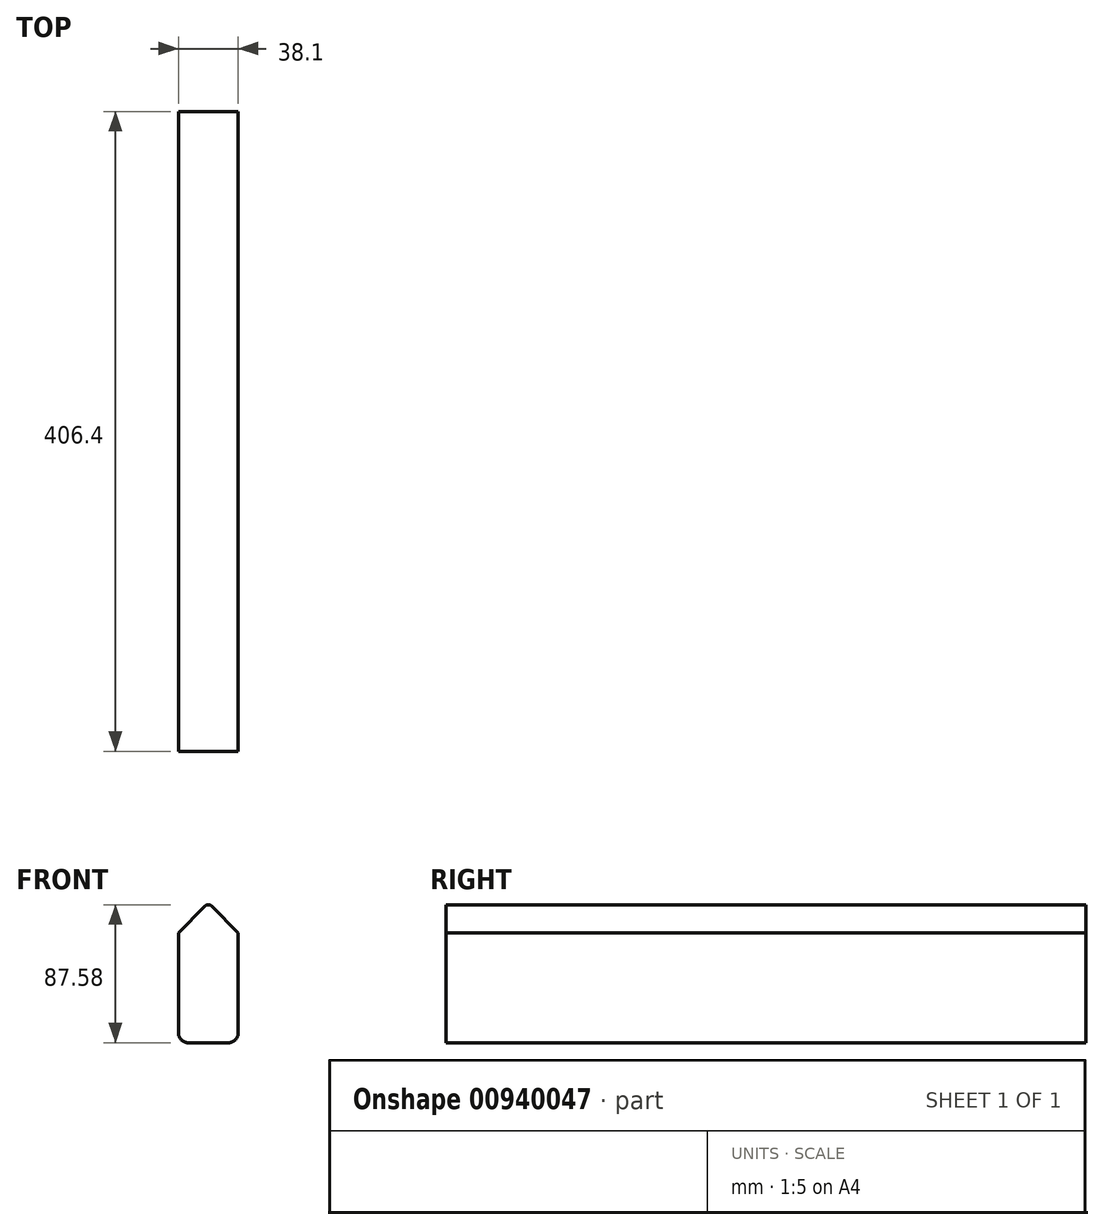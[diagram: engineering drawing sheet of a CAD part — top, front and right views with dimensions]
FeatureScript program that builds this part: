
annotation { "Feature Type Name" : "Feature", "Feature Type Description" : "" }
export const myFeature = defineFeature(function(context is Context, id is Id, definition is map)
    precondition{}
    {
        {
            var Q0;
            Q0=qCreatedBy(makeId("Front.planeOp"),FACE);
            var sketch = newSketch(context, id + "F0", { "sketchPlane" : qUnion([Q0])});
            skLineSegment(sketch, "E0.top", {"start": v(12.7, -44.45) * mm, "end": v(-12.7, -44.45) * mm});
            skLineSegment(sketch, "E0.left", {"start": v(19.05, 25.4) * mm, "end": v(19.05, -38.1) * mm});
            skLineSegment(sketch, "E0.right", {"start": v(-19.05, 25.4) * mm, "end": v(-19.05, -38.1) * mm});
            skPoint(sketch, "E0.middle", {"position": v(0, 0) * mm});
            skPoint(sketch, "E1.visualSharp", {"position": v(-19.05, -44.45) * mm});
            skArc(sketch, "E1.filletArc", {"start": v(-19.05, -38.1) * mm, "mid": v(-17.2, -42.6) * mm, "end": v(-12.7, -44.45) * mm});
            skPoint(sketch, "E2.visualSharp", {"position": v(19.05, -44.45) * mm});
            skArc(sketch, "E2.filletArc", {"start": v(12.7, -44.45) * mm, "mid": v(17.2, -42.6) * mm, "end": v(19.05, -38.1) * mm});
            skLineSegment(sketch, "E3", {"start": v(2.25, 42.2) * mm, "end": v(19.05, 25.4) * mm});
            skLineSegment(sketch, "E4", {"start": v(-2.25, 42.2) * mm, "end": v(-19.05, 25.4) * mm});
            skArc(sketch, "E5.filletArc", {"start": v(2.25, 42.2) * mm, "mid": v(0, 43.13) * mm, "end": v(-2.25, 42.2) * mm});
            skSolve(sketch);
        }
        {
            var Q0;
            Q0 = qSketchRegion(id + "F0", true);
            extrude(context, id + "F1", {"entities" : qUnion([Q0]), "depth" : 406.4 * mm, "offsetDistance" : 25.4 * mm});
        }
    });
